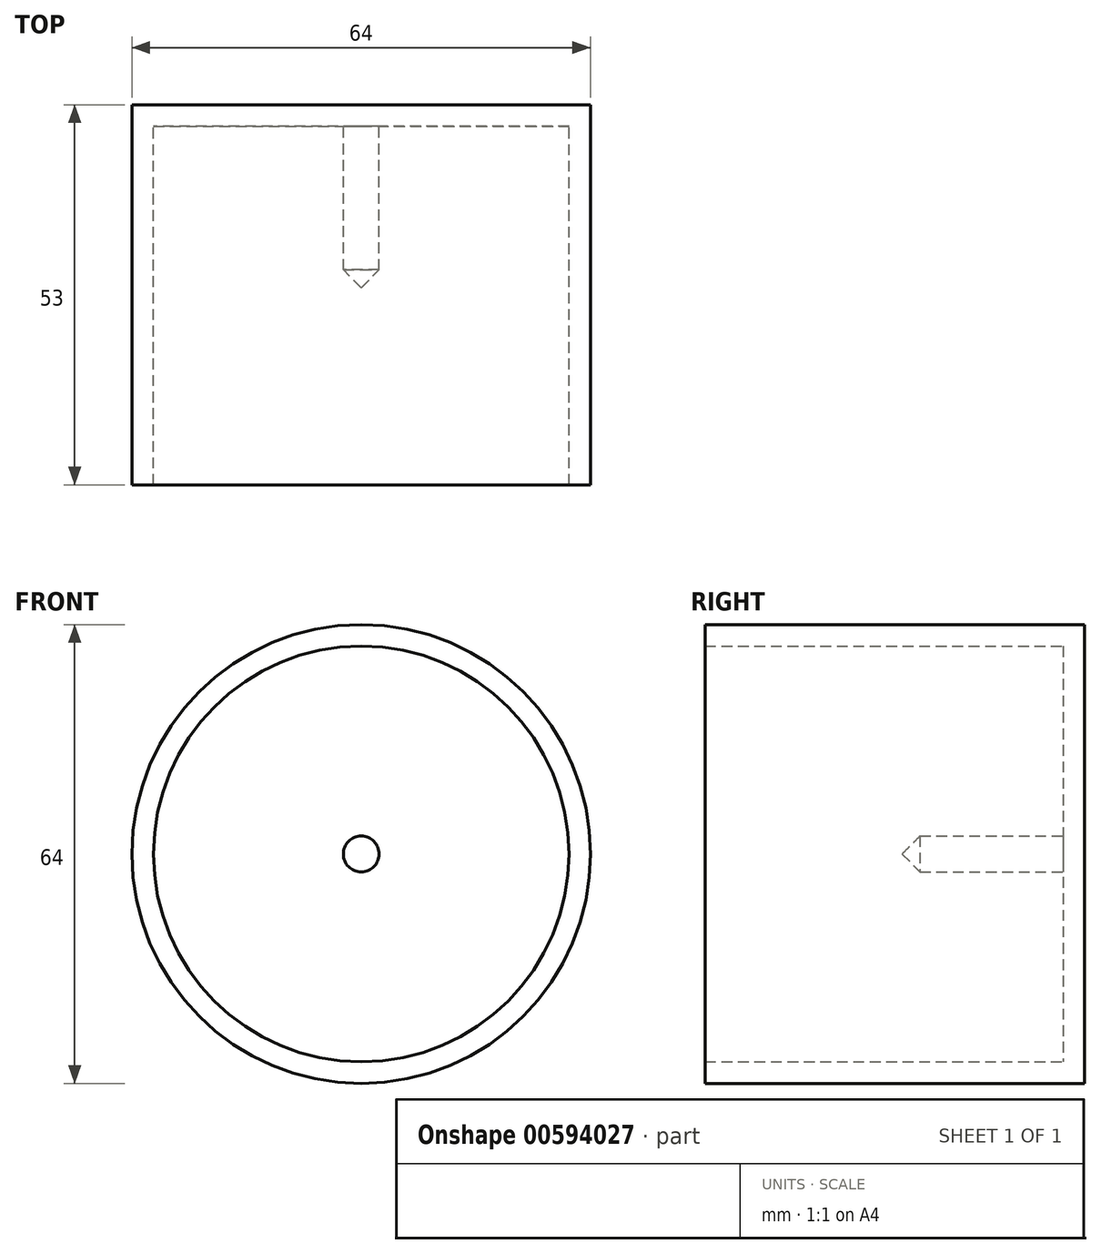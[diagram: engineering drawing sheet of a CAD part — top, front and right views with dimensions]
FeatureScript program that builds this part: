
annotation { "Feature Type Name" : "Feature", "Feature Type Description" : "" }
export const myFeature = defineFeature(function(context is Context, id is Id, definition is map)
    precondition{}
    {
        {
            var Q0;
            Q0=qCreatedBy(makeId("Top.planeOp"),FACE);
            var sketch = newSketch(context, id + "F0", { "sketchPlane" : qUnion([Q0])});
            skLineSegment(sketch, "E0", {"start": v(0, 0) * mm, "end": v(0, 0) * mm});
            skLineSegment(sketch, "E1", {"start": v(0, -25.5) * mm, "end": v(0, -51) * mm, "construction": true});
            skLineSegment(sketch, "E2.bottom", {"start": v(0, 0) * mm, "end": v(32, 0) * mm});
            skLineSegment(sketch, "E2.top", {"start": v(2.5, -3) * mm, "end": v(29, -3) * mm});
            skLineSegment(sketch, "E2.left", {"start": v(0, 0) * mm, "end": v(0, -3) * mm});
            skLineSegment(sketch, "E2.right", {"start": v(32, 0) * mm, "end": v(32, -3) * mm});
            skLineSegment(sketch, "E3.top", {"start": v(32, -53) * mm, "end": v(29, -53) * mm});
            skLineSegment(sketch, "E3.left", {"start": v(32, -3) * mm, "end": v(32, -53) * mm});
            skLineSegment(sketch, "E3.right", {"start": v(29, -3) * mm, "end": v(29, -53) * mm});
            skLineSegment(sketch, "E4.left", {"start": v(0, 0) * mm, "end": v(0, -25.5) * mm});
            skLineSegment(sketch, "E4.right", {"start": v(2.5, -3) * mm, "end": v(2.5, -23) * mm});
            skLineSegment(sketch, "E5", {"start": v(2.5, -23) * mm, "end": v(0, -25.5) * mm});
            skPoint(sketch, "E6.orphan", {"position": v(0, -23) * mm});
            skSolve(sketch);
        }
        {
            var Q0;
            {var subQ0=sQuery(id+"F0.wireOp",EDGE,"E2.bottom");Q0=makeQuery(id+"F0.imprint","IMPRINT",FACE,{"disambiguationData":[TD([[makeQuery(id+"F0.imprint","IMPRINT",EDGE,{"derivedFrom":subQ0}),-1.0]])]});}
            var Q1;
            Q1=sQuery(id+"F0.wireOp",EDGE,"E1");
            revolve(context, id + "F1", {"entities" : qUnion([Q0]), "axis" : qUnion([Q1]), "revolveType" : RevolveType.FULL});
        }
    });
